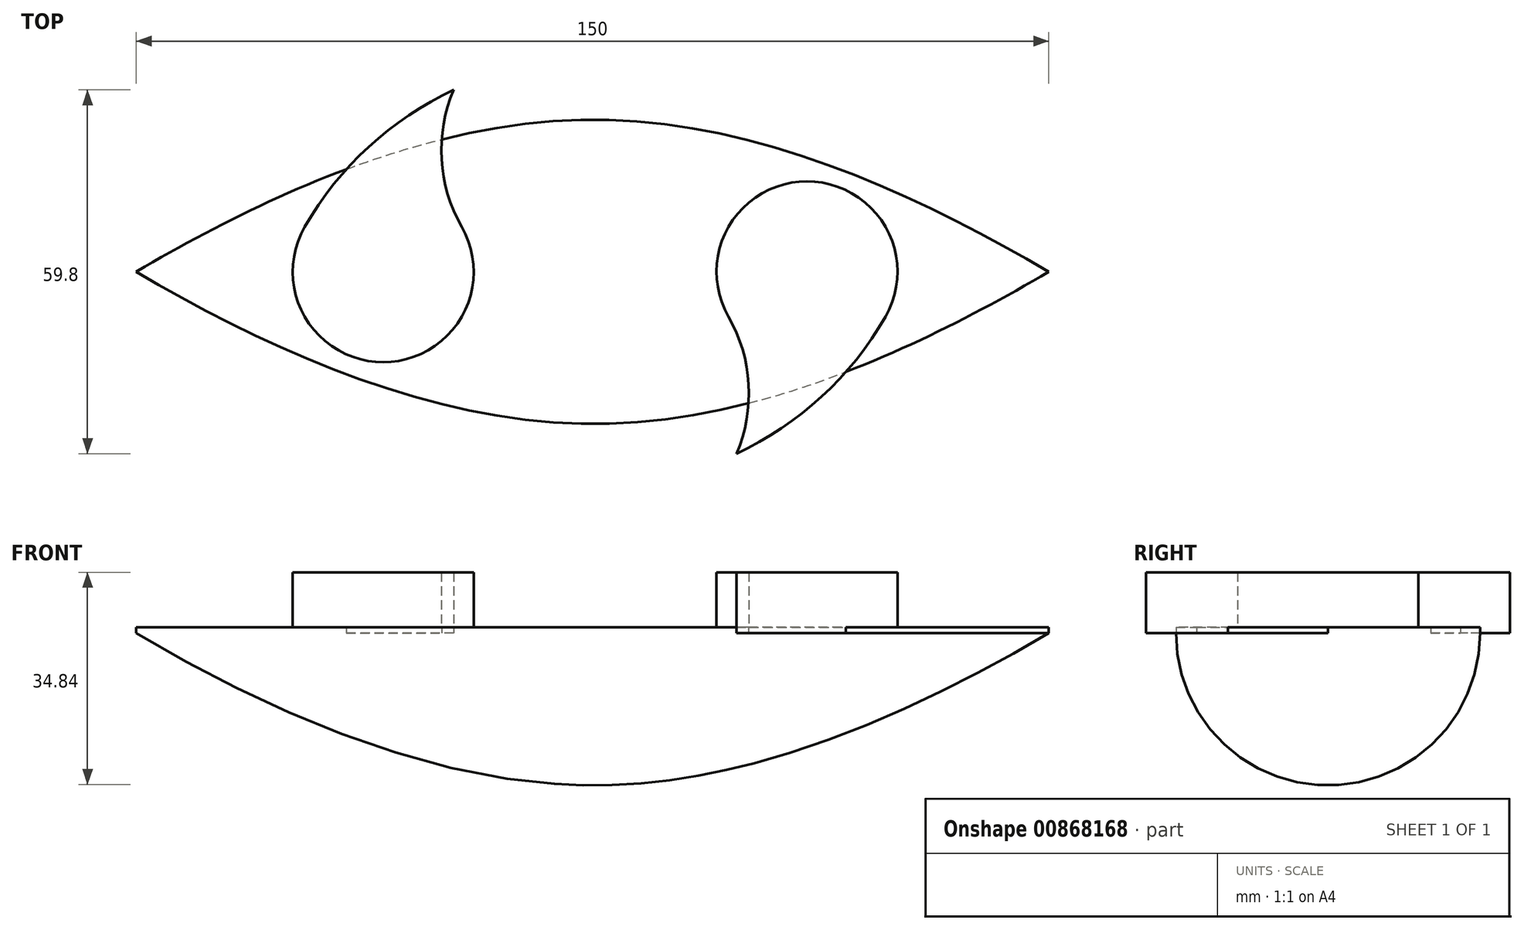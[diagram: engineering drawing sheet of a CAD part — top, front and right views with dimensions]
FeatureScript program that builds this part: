
annotation { "Feature Type Name" : "Feature", "Feature Type Description" : "" }
export const myFeature = defineFeature(function(context is Context, id is Id, definition is map)
    precondition{}
    {
        {
            var Q0;
            Q0=qCreatedBy(makeId("Front.planeOp"),FACE);
            var sketch = newSketch(context, id + "F0", { "sketchPlane" : qUnion([Q0])});
            skFitSpline(sketch, "E0", {"points": [v(-75.42, 0) * mm, v(0, -25) * mm, v(74.58, 0) * mm], "startDerivative": vector(126.95, -75.06) * mm, "endDerivative": vector(128.09, 74.94) * mm});
            skLineSegment(sketch, "E1", {"start": v(-75.42, 0) * mm, "end": v(74.58, 0) * mm});
            skSolve(sketch);
        }
        {
            var Q0;
            Q0 = qSketchRegion(id + "F0", true);
            var Q1;
            Q1=sQuery(id+"F0.wireOp",EDGE,"E1");
            revolve(context, id + "F1", {"surfaceOperationType" : NewSurfaceOperationType.NEW, "entities" : qUnion([Q0]), "axis" : qUnion([Q1]), "revolveType" : RevolveType.SYMMETRIC, "angle" : 180 * degree});
        }
        {
            var Q0;
            Q0=makeQuery(id+"F1.opRevolve","CAP_FACE",FACE,{"disambiguationData":[OSD([sQuery(id+"F0.wireOp",EDGE,"E0"),sQuery(id+"F0.wireOp",EDGE,"E1")])],"isStart":false});
            var sketch = newSketch(context, id + "F2", { "sketchPlane" : qUnion([Q0])});
            skArc(sketch, "E2", {"start": v(-47.72, 7.4) * mm, "mid": v(-34.83, -14.87) * mm, "end": v(-21.93, 7.4) * mm});
            skArc(sketch, "E3", {"start": v(47.72, -7.4) * mm, "mid": v(34.83, 14.87) * mm, "end": v(21.93, -7.4) * mm});
            skCircle(sketch, "E4", {"center": v(0, 0) * mm, "radius": 19.96 * mm, "construction": true});
            skCircle(sketch, "E5", {"center": v(0, 0) * mm, "radius": 49.7 * mm, "construction": true});
            skArc(sketch, "E6", {"start": v(-23.24, 29.9) * mm, "mid": v(-37.22, 20.54) * mm, "end": v(-47.72, 7.4) * mm});
            skArc(sketch, "E7", {"start": v(23.24, -29.9) * mm, "mid": v(25.23, -18.49) * mm, "end": v(21.93, -7.4) * mm});
            skArc(sketch, "E8.trimOffspring", {"start": v(-23.24, 29.9) * mm, "mid": v(-25.23, 18.49) * mm, "end": v(-21.93, 7.4) * mm});
            skArc(sketch, "E9.trimOffspring", {"start": v(23.24, -29.9) * mm, "mid": v(37.22, -20.54) * mm, "end": v(47.72, -7.4) * mm});
            skSolve(sketch);
        }
        {
            var Q0;
            {var subQ0=sQuery(id+"F2.wireOp",EDGE,"E8.trimOffspring");var subQ1=sQuery(id+"F2.wireOp",EDGE,"E6");var subQ2=makeQuery(id+"F2.imprint","INTERSECT",VERTEX,{"derivedFrom":[subQ1,subQ0]});Q0=makeQuery(id+"F2.imprint","IMPRINT",FACE,{"disambiguationData":[TD([[makeQuery(id+"F2.imprint","IMPRINT",EDGE,{"disambiguationData":[TD([[subQ2,-1.0]])],"derivedFrom":subQ1}),1.0]])]});}
            var Q1;
            {var subQ0=sQuery(id+"F2.wireOp",EDGE,"E2");Q1=makeQuery(id+"F2.imprint","IMPRINT",FACE,{"disambiguationData":[TD([[makeQuery(id+"F2.imprint","IMPRINT",EDGE,{"derivedFrom":subQ0}),1.0]])]});}
            var Q2;
            {var subQ0=sQuery(id+"F2.wireOp",EDGE,"E3");Q2=makeQuery(id+"F2.imprint","IMPRINT",FACE,{"disambiguationData":[TD([[makeQuery(id+"F2.imprint","IMPRINT",EDGE,{"derivedFrom":subQ0}),1.0]])]});}
            var Q3;
            {var subQ0=sQuery(id+"F2.wireOp",EDGE,"E9.trimOffspring");var subQ1=sQuery(id+"F2.wireOp",EDGE,"E7");var subQ2=makeQuery(id+"F2.imprint","INTERSECT",VERTEX,{"derivedFrom":[subQ1,subQ0]});Q3=makeQuery(id+"F2.imprint","IMPRINT",FACE,{"disambiguationData":[TD([[makeQuery(id+"F2.imprint","IMPRINT",EDGE,{"disambiguationData":[TD([[subQ2,-1.0]])],"derivedFrom":subQ1}),-1.0]])]});}
            extrude(context, id + "F3", {"entities" : qUnion([Q0, Q1, Q2, Q3]), "operationType" : NewBodyOperationType.ADD, "depth" : 10 * mm, "offsetDistance" : 25 * mm});
        }
        {
            var Q0;
            Q0=makeQuery(id+"F1.opRevolve","CAP_FACE",FACE,{"disambiguationData":[OSD([sQuery(id+"F0.wireOp",EDGE,"E0"),sQuery(id+"F0.wireOp",EDGE,"E1")])],"isStart":false});
            extrude(context, id + "F4", {"entities" : qUnion([Q0]), "operationType" : NewBodyOperationType.ADD, "depth" : 1 * mm, "offsetDistance" : 25 * mm});
        }
    });
